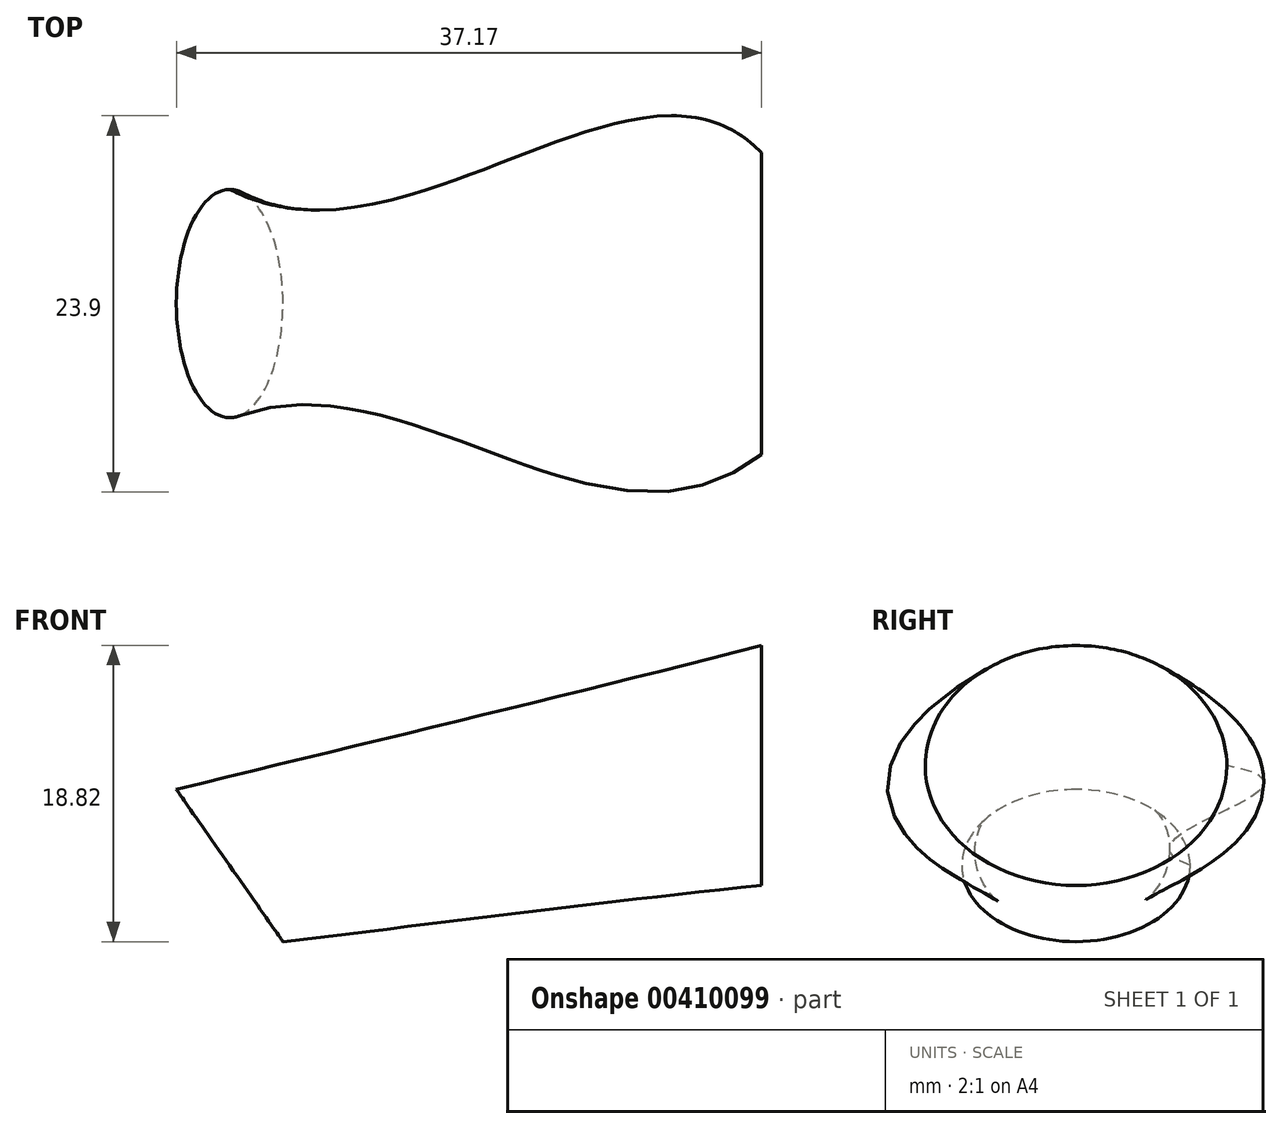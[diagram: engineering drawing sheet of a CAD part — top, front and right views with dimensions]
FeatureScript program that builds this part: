
annotation { "Feature Type Name" : "Feature", "Feature Type Description" : "" }
export const myFeature = defineFeature(function(context is Context, id is Id, definition is map)
    precondition{}
    {
        {
            var Q0;
            Q0=qCreatedBy(makeId("Top.planeOp"),FACE);
            var sketch = newSketch(context, id + "F0", { "sketchPlane" : qUnion([Q0])});
            skEllipticalArc(sketch, "E0", {});
            skEllipticalArc(sketch, "E1", {});
            skEllipticalArc(sketch, "E2", {});
            skEllipticalArc(sketch, "E3", {});
            const initialGuessF0  = {"E0": [-0.006375392586737872, 0, 1, 0, 0.0127, 0.0127, 3.141592653589793, 4.71238898038469], "E1": [-0.006375392586737872, 0, 1, 0, 0.0127, 0.0127, 0, 1.5707963267948966], "E2": [-0.006375392586737872, 0, 1, 0, 0.0127, 0.0127, 1.5707963267948966, 3.141592653589793], "E3": [-0.006375392586737872, 0, 1, 0, 0.0127, 0.0127, 4.71238898038469, 0]};
            skSetInitialGuess(sketch, initialGuessF0);
            skSolve(sketch);
        }
        {
            var Q0;
            Q0=qCreatedBy(makeId("Right.planeOp"),FACE);
            cPlane(context, id + "F1", {"entities" : qUnion([Q0]), "cplaneType" : CPlaneType.OFFSET, "offset" : 15 * mm, "width" : 152.4 * mm, "height" : 152.4 * mm});
        }
        {
            var Q0;
            Q0=qCreatedBy(id+"F1.planeOp",FACE);
            var sketch = newSketch(context, id + "F2", { "sketchPlane" : qUnion([Q0])});
            skLineSegment(sketch, "E4", {"start": v(-8.4, 0) * mm, "end": v(8.06, 0) * mm});
            skSolve(sketch);
        }
        {
            var Q0;
            Q0=sQuery(id+"F2.wireOp",EDGE,"E4");
            cPlane(context, id + "F3", {"entities" : qUnion([Q0]), "cplaneType" : CPlaneType.LINE_ANGLE, "offset" : 25.4 * mm, "angle" : 55 * degree, "width" : 152.4 * mm, "height" : 152.4 * mm});
        }
        {
            var Q0;
            Q0=qCreatedBy(id+"F3.planeOp",FACE);
            var sketch = newSketch(context, id + "F4", { "sketchPlane" : qUnion([Q0])});
            skEllipticalArc(sketch, "E5", {});
            skEllipticalArc(sketch, "E6", {});
            skEllipticalArc(sketch, "E7", {});
            skEllipticalArc(sketch, "E8", {});
            skLineSegment(sketch, "E9", {"start": v(0, -8.73) * mm, "end": v(0, 31.2) * mm, "construction": true});
            const initialGuessF4  = {"E5": [0, 0.010009883524843222, 1, 0, 0.0072517, 0.005905500000000001, 3.141592653589793, 4.71238898038469], "E6": [0, 0.010009883524843222, 1, 0, 0.0072517, 0.005905500000000001, 1.5707963267948966, 3.141592653589793], "E7": [0, 0.010009883524843222, 1, 0, 0.0072517, 0.005905500000000001, 0, 1.5707963267948966], "E8": [0, 0.010009883524843222, 1, 0, 0.0072517, 0.005905500000000001, 4.71238898038469, 0]};
            skSetInitialGuess(sketch, initialGuessF4);
            skSolve(sketch);
        }
        {
            var Q0;
            Q0=qCreatedBy(makeId("Right.planeOp"),FACE);
            cPlane(context, id + "F5", {"entities" : qUnion([Q0]), "cplaneType" : CPlaneType.OFFSET, "offset" : 38.1 * mm, "width" : 152.4 * mm, "height" : 152.4 * mm});
        }
        {
            var Q0;
            Q0=qCreatedBy(id+"F5.planeOp",FACE);
            var sketch = newSketch(context, id + "F6", { "sketchPlane" : qUnion([Q0])});
            skEllipticalArc(sketch, "E10", {});
            skEllipticalArc(sketch, "E11", {});
            skEllipticalArc(sketch, "E12", {});
            skEllipticalArc(sketch, "E13", {});
            skLineSegment(sketch, "E14", {"start": v(0, 7.18) * mm, "end": v(0, 39.23) * mm, "construction": true});
            const initialGuessF6  = {"E10": [0, 0.021596454083919525, 1, 0, 0.0095758, 0.00762, 3.141592653589793, 4.71238898038469], "E11": [0, 0.021596454083919525, 1, 0, 0.0095758, 0.00762, 0, 1.5707963267948966], "E12": [0, 0.021596454083919525, 1, 0, 0.0095758, 0.00762, 1.5707963267948966, 3.141592653589793], "E13": [0, 0.021596454083919525, 1, 0, 0.0095758, 0.00762, 4.71238898038469, 0]};
            skSetInitialGuess(sketch, initialGuessF6);
            skSolve(sketch);
        }
        {
            var Q0;
            Q0=qCreatedBy(makeId("Right.planeOp"),FACE);
            cPlane(context, id + "F7", {"entities" : qUnion([Q0]), "cplaneType" : CPlaneType.OFFSET, "offset" : 68.83 * mm, "width" : 152.4 * mm, "height" : 152.4 * mm});
        }
        {
            var Q0;
            Q0=qCreatedBy(id+"F7.planeOp",FACE);
            var sketch = newSketch(context, id + "F8", { "sketchPlane" : qUnion([Q0])});
            skEllipticalArc(sketch, "E15", {});
            skEllipticalArc(sketch, "E16", {});
            skEllipticalArc(sketch, "E17", {});
            skEllipticalArc(sketch, "E18", {});
            skLineSegment(sketch, "E19", {"start": v(-14.1, 0) * mm, "end": v(19.06, 0) * mm, "construction": true});
            skLineSegment(sketch, "E20", {"start": v(-12.56, 22.8) * mm, "end": v(12.4, 22.8) * mm, "construction": true});
            const initialGuessF8  = {"E15": [0, 0.022809816524386406, 1, 0, 0.008445500000000002, 0.00635, 1.5707963267948966, 3.141592653589793], "E16": [0, 0.022809816524386406, 1, 0, 0.008445500000000002, 0.00635, 0, 1.5707963267948966], "E17": [0, 0.022809816524386406, 1, 0, 0.008445500000000002, 0.00635, 4.71238898038469, 0], "E18": [0, 0.022809816524386406, 1, 0, 0.008445500000000002, 0.00635, 3.141592653589793, 4.71238898038469]};
            skSetInitialGuess(sketch, initialGuessF8);
            skSolve(sketch);
        }
        {
            var Q0;
            Q0=sQuery(id+"F4.wireOp",VERTEX,"E8.start");
            var Q1;
            Q1=sQuery(id+"F4.wireOp",VERTEX,"E7.end");
            var Q2;
            Q2=sQuery(id+"F6.wireOp",VERTEX,"E10.center");
            cPlane(context, id + "F9", {"entities" : qUnion([Q0, Q1, Q2]), "cplaneType" : CPlaneType.THREE_POINT, "offset" : 25.4 * mm, "width" : 152.4 * mm, "height" : 152.4 * mm});
        }
        {
            var Q0;
            Q0=qCreatedBy(id+"F9.planeOp",FACE);
            var sketch = newSketch(context, id + "F10", { "sketchPlane" : qUnion([Q0])});
            skPoint(sketch, "E21.0.internal.orphan", {"position": v(6.32, 0) * mm});
            skPoint(sketch, "E22.0.internal.orphan", {"position": v(-19.08, 0) * mm});
            skPoint(sketch, "E22.1.internal.orphan", {"position": v(0.93, 20.08) * mm});
            skPoint(sketch, "E22.2.internal.orphan", {"position": v(38.1, 29.22) * mm});
            skPoint(sketch, "E22.3.internal.orphan", {"position": v(68.83, 29.16) * mm});
            skPoint(sketch, "E23.1.internal.orphan", {"position": v(7.7, 10.4) * mm});
            skPoint(sketch, "E23.2.internal.orphan", {"position": v(38.1, 13.98) * mm});
            skPoint(sketch, "E23.3.internal.orphan", {"position": v(68.83, 16.46) * mm});
            skFitSpline(sketch, "E24", {"points": [v(0.93, 20.08) * mm, v(38.1, 29.22) * mm], "startDerivative": vector(11.06, 44.33) * mm, "endDerivative": vector(38.18, -3.7) * mm});
            skFitSpline(sketch, "E25", {"points": [v(7.7, 10.4) * mm, v(38.1, 13.98) * mm], "startDerivative": vector(28.69, 16.59) * mm, "endDerivative": vector(19.78, 28.64) * mm});
            skSolve(sketch);
        }
        {
            var Q0;
            Q0=sQuery(id+"F4.wireOp",VERTEX,"E6.end");
            var Q1;
            Q1=sQuery(id+"F4.wireOp",VERTEX,"E8.end");
            var Q2;
            Q2=sQuery(id+"F6.wireOp",VERTEX,"E13.center");
            cPlane(context, id + "F11", {"entities" : qUnion([Q0, Q1, Q2]), "cplaneType" : CPlaneType.THREE_POINT, "offset" : 25.4 * mm, "width" : 152.4 * mm, "height" : 152.4 * mm});
        }
        {
            var Q0;
            Q0=qCreatedBy(id+"F11.planeOp",FACE);
            var sketch = newSketch(context, id + "F12", { "sketchPlane" : qUnion([Q0])});
            skPoint(sketch, "E26.0", {"position": v(7.06, 7.25) * mm});
            skPoint(sketch, "E27.0", {"position": v(41.44, 9.58) * mm});
            skPoint(sketch, "E28.0", {"position": v(41.44, -9.58) * mm});
            skPoint(sketch, "E29.0", {"position": v(7.06, -7.25) * mm});
            skFitSpline(sketch, "E30", {"points": [v(7.06, 7.25) * mm, v(41.44, 9.58) * mm], "startDerivative": vector(34.88, -17.75) * mm, "endDerivative": vector(24.37, -24.69) * mm});
            skFitSpline(sketch, "E31", {"points": [v(7.06, -7.25) * mm, v(41.44, -9.58) * mm], "startDerivative": vector(35.59, 13.15) * mm, "endDerivative": vector(31.38, 23.77) * mm});
            skSolve(sketch);
        }
        {
            var Q0;
            Q0=makeQuery(id+"F4.imprint","IMPRINT",FACE,{"disambiguationData":[TD([[makeQuery(id+"F4.imprint","IMPRINT",EDGE,{"derivedFrom":sQuery(id+"F4.wireOp",EDGE,"E5")}),1.0]])]});
            var Q1;
            Q1=makeQuery(id+"F6.imprint","IMPRINT",FACE,{"disambiguationData":[TD([[makeQuery(id+"F6.imprint","IMPRINT",EDGE,{"derivedFrom":sQuery(id+"F6.wireOp",EDGE,"E10")}),1.0]])]});
            var Q2;
            Q2=sQuery(id+"F0.wireOp",EDGE,"E0");
            var Q3;
            Q3=sQuery(id+"F4.wireOp",EDGE,"E6");
            var Q4;
            Q4=sQuery(id+"F6.wireOp",EDGE,"E12");
            var Q5;
            Q5=sQuery(id+"F8.wireOp",EDGE,"E15");
            var Q6;
            Q6=sQuery(id+"F12.wireOp",EDGE,"E30");
            var Q7;
            Q7=sQuery(id+"F12.wireOp",EDGE,"E31");
            var Q8;
            Q8=sQuery(id+"F10.wireOp",VERTEX,"aa9861bf-1fb1-4be0-b845-59ba3e6af564.0");
            var Q9;
            Q9=sQuery(id+"F10.wireOp",VERTEX,"bdc59c72-19d5-4132-b296-d01d35053aa6.0");
            loft(context, id + "F13", {"addGuides" : true, "sheetProfilesArray" : [{ "sheetProfileEntities" : qUnion([Q0]) }, { "sheetProfileEntities" : qUnion([Q1]) }], "wireProfilesArray" : [{ "wireProfileEntities" : qUnion([Q2]) }, { "wireProfileEntities" : qUnion([Q3]) }, { "wireProfileEntities" : qUnion([Q4]) }, { "wireProfileEntities" : qUnion([Q5]) }], "guidesArray" : [{ "guideEntities" : qUnion([Q6]), "guideDerivativeType" : LoftGuideDerivativeType.DEFAULT, "guideDerivativeMagnitude" : 1 }, { "guideEntities" : qUnion([Q7]), "guideDerivativeType" : LoftGuideDerivativeType.DEFAULT, "guideDerivativeMagnitude" : 1 }], "connections" : [{ "connectionEntities" : qUnion([Q8, Q9]), "connectionEdgeQueries" : qUnion([]), "connectionEdgeParameters" : [] }]});
        }
    });
